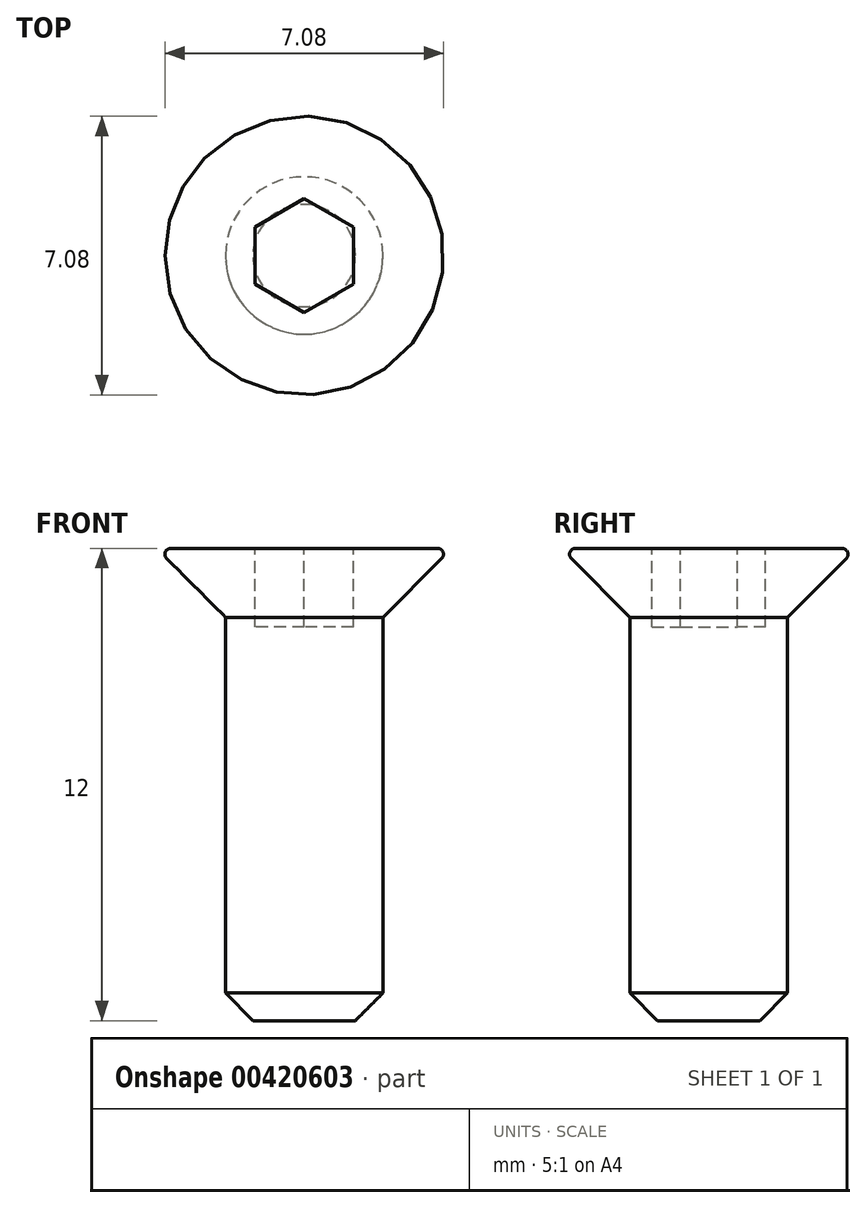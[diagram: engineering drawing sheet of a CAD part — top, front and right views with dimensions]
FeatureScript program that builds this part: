
annotation { "Feature Type Name" : "Feature", "Feature Type Description" : "" }
export const myFeature = defineFeature(function(context is Context, id is Id, definition is map)
    precondition{}
    {
        {
            var Q0;
            Q0=qCreatedBy(makeId("Front.planeOp"),FACE);
            var sketch = newSketch(context, id + "F0", { "sketchPlane" : qUnion([Q0])});
            skLineSegment(sketch, "E0", {"start": v(0, 0) * mm, "end": v(0, 31.51) * mm, "construction": true});
            skLineSegment(sketch, "E1", {"start": v(-2, 0) * mm, "end": v(0, 0) * mm});
            skLineSegment(sketch, "E2", {"start": v(0, 12) * mm, "end": v(-3.75, 12) * mm});
            skLineSegment(sketch, "E3", {"start": v(-3.75, 12) * mm, "end": v(-2, 10.25) * mm});
            skLineSegment(sketch, "E4", {"start": v(-2, 10.25) * mm, "end": v(-2, 0) * mm});
            skLineSegment(sketch, "E5", {"start": v(0, 12) * mm, "end": v(0, 0) * mm});
            skSolve(sketch);
        }
        {
            var Q0;
            Q0 = qSketchRegion(id + "F0", true);
            var Q1;
            Q1=sQuery(id+"F0.wireOp",EDGE,"E0");
            revolve(context, id + "F1", {"entities" : qUnion([Q0]), "axis" : qUnion([Q1]), "revolveType" : RevolveType.FULL});
        }
        {
            var Q0;
            Q0=makeQuery(id+"F1.opRevolve","SWEPT_EDGE",EDGE,{"disambiguationData":[OSD([sQuery(id+"F0.wireOp",EDGE,"E1"),sQuery(id+"F0.wireOp",EDGE,"E4")])]});
            chamfer(context, id + "F2", {"entities" : qUnion([Q0]), "width" : 0.7 * mm, "tangentPropagation" : true});
        }
        {
            var Q0;
            Q0=makeQuery(id+"F1.opRevolve","SWEPT_FACE",FACE,{"disambiguationData":[OSD([sQuery(id+"F0.wireOp",EDGE,"E2")])]});
            var sketch = newSketch(context, id + "F3", { "sketchPlane" : qUnion([Q0])});
            skCircle(sketch, "E6.cCircle", {"center": v(0, 0) * mm, "radius": 1.25 * mm, "construction": true});
            skLineSegment(sketch, "E6.0", {"start": v(-1.25, -0.72) * mm, "end": v(-1.25, 0.72) * mm});
            skLineSegment(sketch, "E6.1", {"start": v(-1.25, 0.72) * mm, "end": v(0, 1.44) * mm});
            skLineSegment(sketch, "E6.2", {"start": v(0, 1.44) * mm, "end": v(1.25, 0.72) * mm});
            skLineSegment(sketch, "E6.3", {"start": v(1.25, 0.72) * mm, "end": v(1.25, -0.72) * mm});
            skLineSegment(sketch, "E6.4", {"start": v(1.25, -0.72) * mm, "end": v(0, -1.44) * mm});
            skLineSegment(sketch, "E6.5", {"start": v(0, -1.44) * mm, "end": v(-1.25, -0.72) * mm});
            skPoint(sketch, "E6.0.midPoint", {"position": v(-1.25, 0) * mm});
            skSolve(sketch);
        }
        {
            var Q0;
            Q0 = qSketchRegion(id + "F3", true);
            extrude(context, id + "F4", {"entities" : qUnion([Q0]), "operationType" : NewBodyOperationType.REMOVE, "oppositeDirection" : true, "depth" : 2 * mm, "offsetDistance" : 25 * mm});
        }
        {
            var Q0;
            Q0=makeQuery(id+"F1.opRevolve","SWEPT_EDGE",EDGE,{"disambiguationData":[OSD([sQuery(id+"F0.wireOp",EDGE,"E2"),sQuery(id+"F0.wireOp",EDGE,"E3")])]});
            fillet(context, id + "F5", {"entities" : qUnion([Q0]), "radius" : 0.15 * mm, "tangentPropagation" : true, "allowEdgeOverflow" : false});
        }
    });
